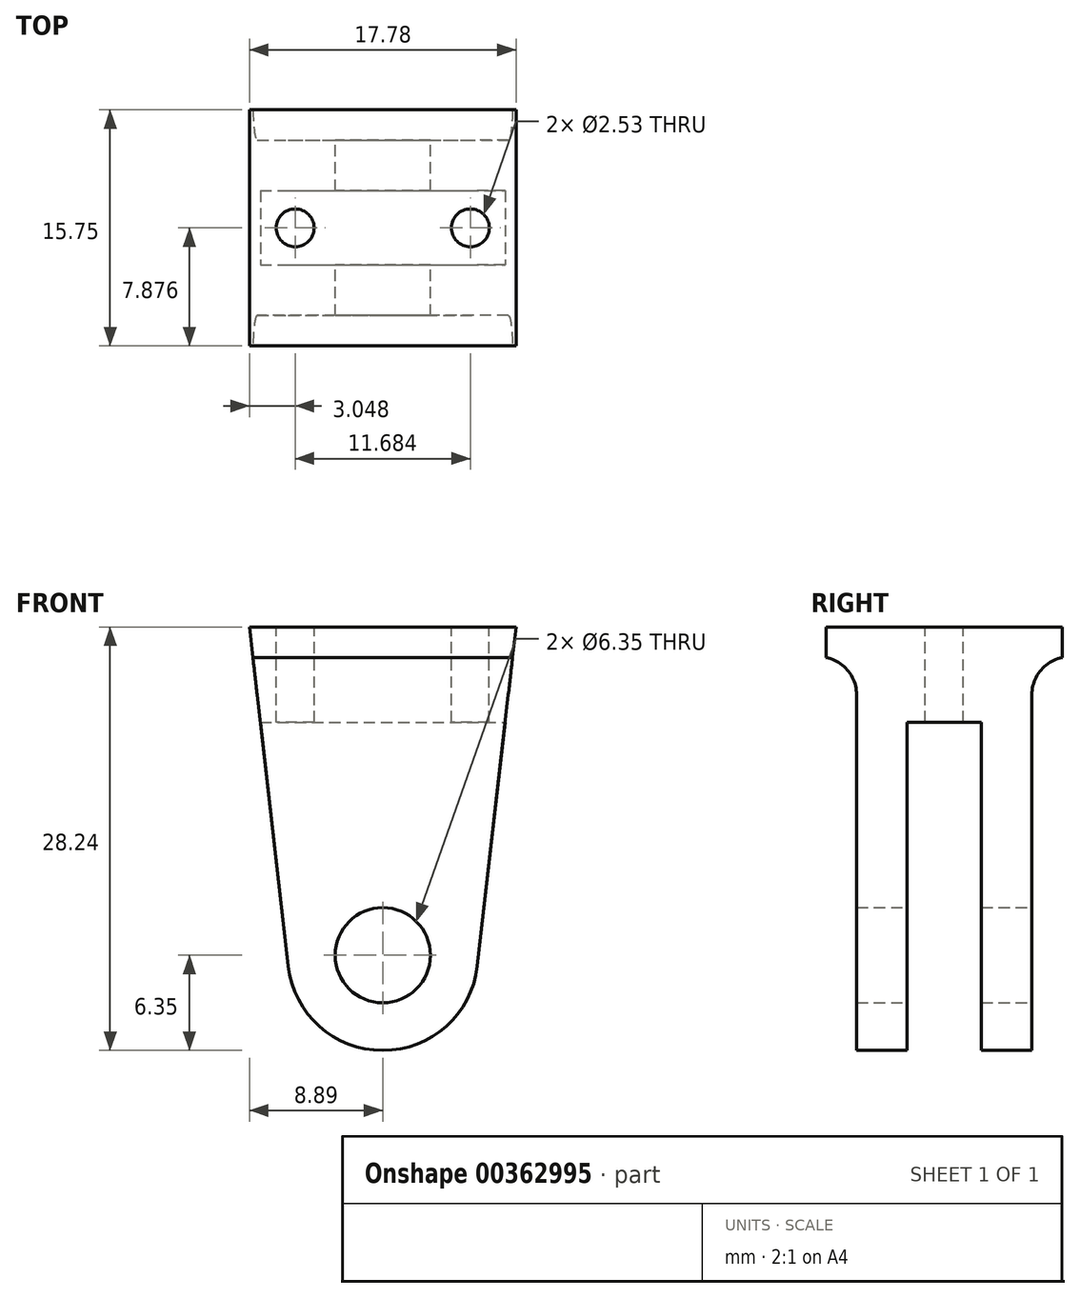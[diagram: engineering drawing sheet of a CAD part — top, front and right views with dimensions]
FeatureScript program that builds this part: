
annotation { "Feature Type Name" : "Feature", "Feature Type Description" : "" }
export const myFeature = defineFeature(function(context is Context, id is Id, definition is map)
    precondition{}
    {
        {
            var Q0;
            Q0=qCreatedBy(makeId("Front.planeOp"),FACE);
            var sketch = newSketch(context, id + "F0", { "sketchPlane" : qUnion([Q0])});
            skCircle(sketch, "E0", {"center": v(0, 0) * mm, "radius": 3.18 * mm});
            skArc(sketch, "E1", {"start": v(-6.3, -0.72) * mm, "mid": v(0, -6.35) * mm, "end": v(6.3, -0.72) * mm});
            skLineSegment(sketch, "E2.0", {"start": v(-8.9, 21.9) * mm, "end": v(8.89, 21.9) * mm});
            skLineSegment(sketch, "E3", {"start": v(-8.9, 21.9) * mm, "end": v(-6.3, -0.72) * mm});
            skLineSegment(sketch, "E4", {"start": v(8.9, 21.9) * mm, "end": v(6.3, -0.72) * mm});
            skSolve(sketch);
        }
        {
            var Q0;
            Q0=makeQuery(id+"F0.imprint","IMPRINT",FACE,{"disambiguationData":[TD([[makeQuery(id+"F0.imprint","IMPRINT",EDGE,{"derivedFrom":sQuery(id+"F0.wireOp",EDGE,"E0")}),-1.0]])]});
            extrude(context, id + "F1", {"entities" : qUnion([Q0]), "depth" : 15.75 * mm});
        }
        {
            var Q0;
            Q0=qCreatedBy(makeId("Right.planeOp"),FACE);
            var sketch = newSketch(context, id + "F2", { "sketchPlane" : qUnion([Q0])});
            skLineSegment(sketch, "E5.0", {"start": v(-15.75, 21.9) * mm, "end": v(0, 21.9) * mm});
            skLineSegment(sketch, "E6.0", {"start": v(-15.75, 21.9) * mm, "end": v(-15.75, -0.72) * mm});
            skLineSegment(sketch, "E7.0.0", {"start": v(0, -0.72) * mm, "end": v(0, 21.9) * mm});
            skLineSegment(sketch, "E7.0.1", {"start": v(0, 21.9) * mm, "end": v(-15.75, 21.9) * mm});
            skLineSegment(sketch, "E7.0.3", {"start": v(-15.75, -0.72) * mm, "end": v(0, -0.72) * mm});
            skPoint(sketch, "E8.endSnap0", {"position": v(-7.87, -0.72) * mm});
            skLineSegment(sketch, "E9.0", {"start": v(-10.35, 15.54) * mm, "end": v(-10.35, -8.71) * mm});
            skLineSegment(sketch, "E10.0", {"start": v(-5.4, 15.54) * mm, "end": v(-5.4, -8.71) * mm});
            skLineSegment(sketch, "E11", {"start": v(-10.35, -8.71) * mm, "end": v(-5.4, -8.71) * mm});
            skLineSegment(sketch, "E12.0", {"start": v(-13.72, 19.86) * mm, "end": v(-13.72, -8.71) * mm});
            skLineSegment(sketch, "E13.0", {"start": v(-2.03, 19.86) * mm, "end": v(-2.03, -8.71) * mm});
            skLineSegment(sketch, "E14.trimOffspring", {"start": v(-5.4, 15.54) * mm, "end": v(-10.35, 15.54) * mm});
            skLineSegment(sketch, "E15", {"start": v(0, -0.72) * mm, "end": v(0, -8.71) * mm});
            skLineSegment(sketch, "E16", {"start": v(0, -8.71) * mm, "end": v(-2.03, -8.71) * mm});
            skLineSegment(sketch, "E17", {"start": v(-15.75, -0.72) * mm, "end": v(-15.75, -8.71) * mm});
            skLineSegment(sketch, "E18", {"start": v(-15.75, -8.71) * mm, "end": v(-13.72, -8.71) * mm});
            skLineSegment(sketch, "E19.0", {"start": v(0, 19.86) * mm, "end": v(-15.75, 19.86) * mm});
            skSolve(sketch);
        }
        {
            var Q0;
            {var subQ5=sQuery(id+"F2.wireOp",EDGE,"E14.trimOffspring");Q0=makeQuery(id+"F2.imprint","IMPRINT",FACE,{"disambiguationData":[TD([[makeQuery(id+"F2.imprint","IMPRINT",EDGE,{"derivedFrom":subQ5}),1.0]])]});}
            var Q1;
            {var subQ5=sQuery(id+"F2.wireOp",EDGE,"E11");Q1=makeQuery(id+"F2.imprint","IMPRINT",FACE,{"disambiguationData":[TD([[makeQuery(id+"F2.imprint","IMPRINT",EDGE,{"derivedFrom":subQ5}),1.0]])]});}
            extrude(context, id + "F3", {"entities" : qUnion([Q0, Q1]), "operationType" : NewBodyOperationType.REMOVE, "endBound" : BoundingType.SYMMETRIC, "oppositeDirection" : true, "depth" : 25.4 * mm});
        }
        {
            var Q0;
            {var subQ0=sQuery(id+"F2.wireOp",EDGE,"E17");Q0=makeQuery(id+"F2.imprint","IMPRINT",FACE,{"disambiguationData":[TD([[makeQuery(id+"F2.imprint","IMPRINT",EDGE,{"derivedFrom":subQ0}),1.0]])]});}
            var Q1;
            {var subQ0=sQuery(id+"F2.wireOp",EDGE,"E15");Q1=makeQuery(id+"F2.imprint","IMPRINT",FACE,{"disambiguationData":[TD([[makeQuery(id+"F2.imprint","IMPRINT",EDGE,{"derivedFrom":subQ0}),-1.0]])]});}
            var Q2;
            {var subQ3=sQuery(id+"F2.wireOp",EDGE,"E19.0");var subQ5=sQuery(id+"F2.wireOp",EDGE,"E13.0");var subQ7=makeQuery(id+"F2.imprint","INTERSECT",VERTEX,{"derivedFrom":[subQ5,subQ3]});Q2=makeQuery(id+"F2.imprint","IMPRINT",FACE,{"disambiguationData":[TD([[makeQuery(id+"F2.imprint","IMPRINT",EDGE,{"disambiguationData":[TD([[subQ7,-1.0]])],"derivedFrom":subQ5}),1.0]])]});}
            var Q3;
            {var subQ3=sQuery(id+"F2.wireOp",EDGE,"E19.0");var subQ5=sQuery(id+"F2.wireOp",EDGE,"E12.0");var subQ7=makeQuery(id+"F2.imprint","INTERSECT",VERTEX,{"derivedFrom":[subQ5,subQ3]});Q3=makeQuery(id+"F2.imprint","IMPRINT",FACE,{"disambiguationData":[TD([[makeQuery(id+"F2.imprint","IMPRINT",EDGE,{"disambiguationData":[TD([[subQ7,-1.0]])],"derivedFrom":subQ5}),-1.0]])]});}
            extrude(context, id + "F4", {"entities" : qUnion([Q0, Q1, Q2, Q3]), "operationType" : NewBodyOperationType.REMOVE, "endBound" : BoundingType.SYMMETRIC, "oppositeDirection" : true, "depth" : 25.4 * mm});
        }
        {
            var Q0;
            Q0=makeQuery(id+"F4.boolean.opBoolean","COPY",EDGE,{"derivedFrom":makeQuery(id+"F4.opExtrude","SWEPT_EDGE",EDGE,{"disambiguationData":[OSD([sQuery(id+"F2.wireOp",EDGE,"E12.0"),sQuery(id+"F2.wireOp",EDGE,"E19.0")])]})});
            var Q1;
            Q1=makeQuery(id+"F4.boolean.opBoolean","COPY",EDGE,{"derivedFrom":makeQuery(id+"F4.opExtrude","SWEPT_EDGE",EDGE,{"disambiguationData":[OSD([sQuery(id+"F2.wireOp",EDGE,"E13.0"),sQuery(id+"F2.wireOp",EDGE,"E19.0")])]})});
            fillet(context, id + "F5", {"entities" : qUnion([Q0, Q1]), "radius" : 2.54 * mm, "tangentPropagation" : true, "allowEdgeOverflow" : false});
        }
        {
            var Q0;
            Q0=makeQuery(id+"F1.opExtrude","SWEPT_FACE",FACE,{"disambiguationData":[OSD([sQuery(id+"F0.wireOp",EDGE,"E2.0")])]});
            var sketch = newSketch(context, id + "F6", { "sketchPlane" : qUnion([Q0])});
            skPoint(sketch, "E20", {"position": v(-5.84, -7.87) * mm});
            skPoint(sketch, "E20.positionSnap0", {"position": v(-8.9, -7.87) * mm});
            skPoint(sketch, "E21", {"position": v(5.84, -7.87) * mm});
            skSolve(sketch);
        }
        {
            var Q0;
            Q0=sQuery(id+"F6.wireOp",VERTEX,"E20");
            var Q1;
            Q1=sQuery(id+"F6.wireOp",VERTEX,"E21");
            var Q2;
            Q2=makeQuery(id+"F1.opExtrude","SWEPT_BODY",BODY,{"disambiguationData":[OSD([sQuery(id+"F0.wireOp",EDGE,"E0"),sQuery(id+"F0.wireOp",EDGE,"E1"),sQuery(id+"F0.wireOp",EDGE,"E2.0"),sQuery(id+"F0.wireOp",EDGE,"E3"),sQuery(id+"F0.wireOp",EDGE,"E4")])]});
            hole(context, id + "F7", {"style" : HoleStyle.SIMPLE, "endStyle" : HoleEndStyle.THROUGH, "standardTappedOrClearance" : lookupTablePath({ "standard" : "ANSI", "size" : "#39 (0.1)", "type" : "Drilled" }), "standardBlindInLast" : lookupTablePath({ "standard" : "ANSI", "size" : "#39", "type" : "Drilled" }), "holeDiameter" : 2.53 * mm, "tappedDepth" : 4.57 * mm, "tapClearance" : 3, "locations" : qUnion([Q0, Q1]), "scope" : qUnion([Q2])});
        }
    });
